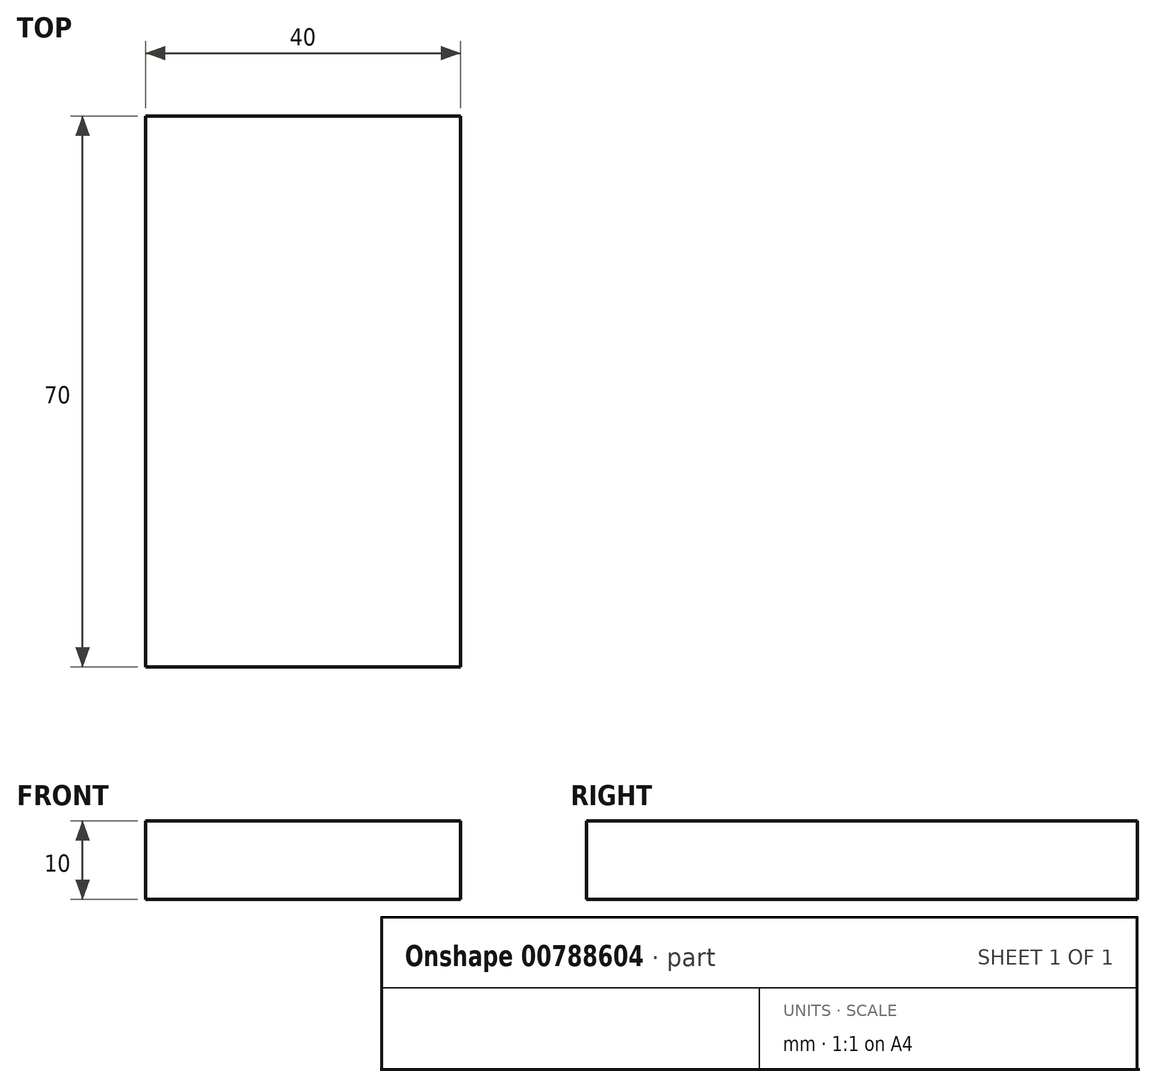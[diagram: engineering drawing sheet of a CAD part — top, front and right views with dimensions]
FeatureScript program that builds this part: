
annotation { "Feature Type Name" : "Feature", "Feature Type Description" : "" }
export const myFeature = defineFeature(function(context is Context, id is Id, definition is map)
    precondition{}
    {
        {
            var Q0;
            Q0=qCreatedBy(makeId("Top.planeOp"),FACE);
            var sketch = newSketch(context, id + "F0", { "sketchPlane" : qUnion([Q0])});
            skLineSegment(sketch, "E0.bottom", {"start": v(-29.31, 41.23) * mm, "end": v(10.69, 41.23) * mm});
            skLineSegment(sketch, "E0.top", {"start": v(-29.31, -28.77) * mm, "end": v(10.69, -28.77) * mm});
            skLineSegment(sketch, "E0.left", {"start": v(-29.31, 41.23) * mm, "end": v(-29.31, -28.77) * mm});
            skLineSegment(sketch, "E0.right", {"start": v(10.69, 41.23) * mm, "end": v(10.69, -28.77) * mm});
            skSolve(sketch);
        }
        {
            var Q0;
            Q0=makeQuery(id+"F0.imprint","IMPRINT",FACE,{"disambiguationData":[TD([[makeQuery(id+"F0.imprint","IMPRINT",EDGE,{"derivedFrom":sQuery(id+"F0.wireOp",EDGE,"E0.bottom")}),-1.0]])]});
            extrude(context, id + "F1", {"entities" : qUnion([Q0]), "depth" : 10 * mm, "offsetDistance" : 25 * mm});
        }
    });
